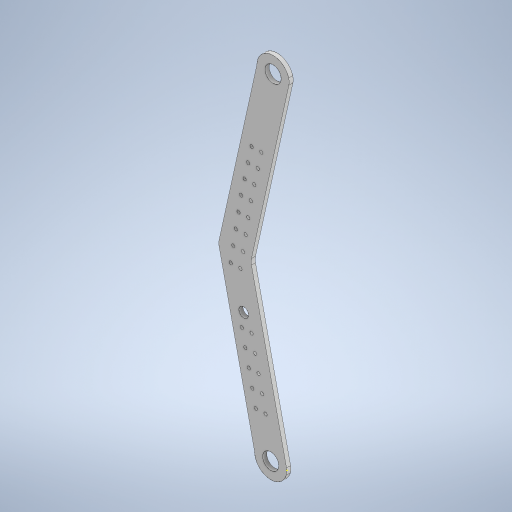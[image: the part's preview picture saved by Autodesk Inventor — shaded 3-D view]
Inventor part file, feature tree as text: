
AUTODESK INVENTOR PART (.ipt)
format: ipt  version: 2023 (Build 270158000, 158)  size: 458,240 bytes
history: native  units: in
note: dims shown in document units (in); Inventor stores cm internally (conversion verified against a paired STEP export)
features: sketch x10, extrude x9, fillet x1, projected_geometry x1
ambient origin geometry x8: Origin, YZ Plane, XZ Plane, XY Plane, X Axis, Y Axis, Z Axis, Center Point
bodies: Body1 (feature_tree)
feature tree (21):
  extrude  "Extrusion3"  Depth=0.7043in
  sketch  "Sketch3"  dims[d0=4.5in d1=0.7043in]
  extrude  "Extrusion14"  Depth=1.0651in
  extrude  "Extrusion15"  Depth=1.0in
  extrude  "Extrusion16"  Depth=0.5in
  extrude  "Extrusion17"  Depth=0.5in
  extrude  "Extrusion18"  Depth=0.5in
  extrude  "Extrusion19"  Depth=1.0in
  extrude  "Extrusion20"  Depth=0.5in
  sketch  "Sketch11"  dims[d25=0.5325in d26=1.0in]
  sketch  "Sketch12"  dims[d27=1.0in d28=0.5in d29=0.5in]
  fillet  "Fillet1"  Radius=0.5in
  sketch  "Sketch13"  dims[d30=0.25in d31=0.0in d42=1.0in]
  extrude  "Extrusion21"  Depth=1.0in
  sketch  "Sketch6"  dims[d2=4.5in d3=1.0651in]
  sketch  "Sketch7"  dims[d4=1.0in d5=1.0in]
  sketch  "Sketch8"  dims[d6=1.0in d7=0.5in]
  projected_geometry  "Projected Loop1"
  sketch  "Sketch9"  dims[d8=0.5in d9=0.5in]
  sketch  "Sketch10"  dims[d10=0.5in d24=5.5in]
  sketch  "Sketch14"  dims[d50=1.5in d51=0.25in d59=0.3in d76=0.585in d77=0.585in d78=1.0in d79=0.0in d82=0.1in d83=1.0in d84=0.0in d89=1.0in d90=0.5325in d91=0.5in d92=0.5in d93=0.5in d94=0.5in d95=0.1in d96=0.1in d97=0.1in d98=0.1in d99=0.1in d100=1.0in d101=0.0in d102=0.6in d103=0.1in d104=1.0in d105=0.0in d106=0.125in d107=0.0in d108=2.0in d109=0.3in d110=0.3in d111=0.3in d112=0.3in d113=0.3in d114=0.3in d115=0.3in d116=0.1in d117=0.1in d118=0.1in d119=0.1in d120=0.1in d121=0.1in d122=0.1in d123=0.5in d124=0.5in d125=0.5in d126=0.5in d127=0.5325in d128=0.5in d129=0.5in d130=0.3in d131=0.3in d132=0.3in d133=0.3in d134=0.3in d135=0.3in d136=0.3in d137=0.1in d138=0.1in d139=0.1in d140=0.1in d141=0.1in d142=0.1in d143=0.1in d144=0.1in d145=0.1in d146=0.1in d147=0.1in d148=0.1in d149=0.1in d150=0.1in d151=0.125in d152=0.0in d153=0.125in d154=0.0in d155=0.4in d156=0.5in d157=0.5in d158=0.125in d159=0.0in d60=0.0344in d61=0.5in d62=0.0344in d74=0.5in d75=0.0344in d80=0.5in d81=0.0344in]
